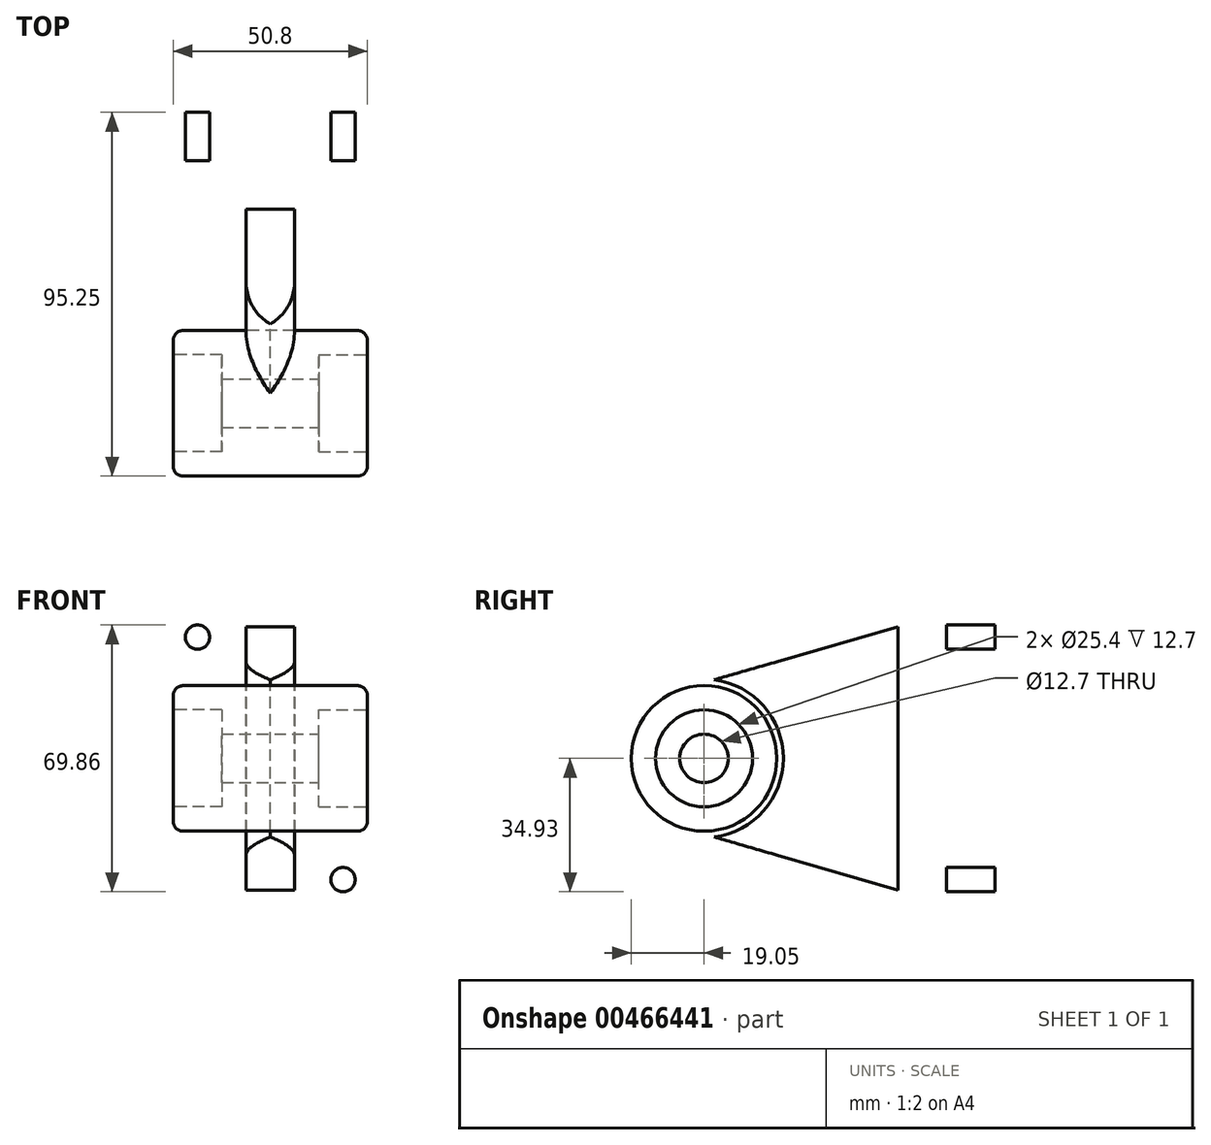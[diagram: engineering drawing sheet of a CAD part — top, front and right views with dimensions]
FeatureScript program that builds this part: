
annotation { "Feature Type Name" : "Feature", "Feature Type Description" : "" }
export const myFeature = defineFeature(function(context is Context, id is Id, definition is map)
    precondition{}
    {
        {
            var Q0;
            Q0=qCreatedBy(makeId("Front.planeOp"),FACE);
            var sketch = newSketch(context, id + "F0", { "sketchPlane" : qUnion([Q0])});
            skLineSegment(sketch, "E0.bottom", {"start": v(-25.4, 38.1) * mm, "end": v(25.4, 38.1) * mm});
            skLineSegment(sketch, "E0.top", {"start": v(-25.4, -38.1) * mm, "end": v(25.4, -38.1) * mm});
            skLineSegment(sketch, "E0.left", {"start": v(-25.4, 38.1) * mm, "end": v(-25.4, -38.1) * mm});
            skLineSegment(sketch, "E0.right", {"start": v(25.4, 38.1) * mm, "end": v(25.4, -38.1) * mm});
            skSolve(sketch);
        }
        {
            var Q0;
            Q0=makeQuery(id+"F0.imprint","IMPRINT",FACE,{"disambiguationData":[TD([[makeQuery(id+"F0.imprint","IMPRINT",EDGE,{"derivedFrom":sQuery(id+"F0.wireOp",EDGE,"E0.bottom")}),-1.0]])]});
            extrude(context, id + "F1", {"entities" : qUnion([Q0]), "depth" : 12.7 * mm});
        }
        {
            var Q0;
            Q0=qCreatedBy(makeId("Right.planeOp"),FACE);
            var sketch = newSketch(context, id + "F2", { "sketchPlane" : qUnion([Q0])});
            skCircle(sketch, "E1", {"center": v(-76.2, 0) * mm, "radius": 19.05 * mm});
            skSolve(sketch);
        }
        {
            var Q0;
            Q0=makeQuery(id+"F2.imprint","IMPRINT",FACE,{"disambiguationData":[TD([[makeQuery(id+"F2.imprint","IMPRINT",EDGE,{"derivedFrom":sQuery(id+"F2.wireOp",EDGE,"E1")}),1.0]])]});
            extrude(context, id + "F3", {"entities" : qUnion([Q0]), "depth" : 25.4 * mm, "hasSecondDirection" : true, "secondDirectionOppositeDirection" : true, "secondDirectionDepth" : 25.4 * mm});
        }
        {
            var Q0;
            Q0=makeQuery(id+"F3.opExtrude","CAP_FACE",FACE,{"disambiguationData":[OSD([sQuery(id+"F2.wireOp",EDGE,"E1")])],"isStart":false});
            var sketch = newSketch(context, id + "F4", { "sketchPlane" : qUnion([Q0])});
            skCircle(sketch, "E2", {"center": v(-76.2, 0) * mm, "radius": 6.35 * mm});
            skCircle(sketch, "E3", {"center": v(-76.2, 0) * mm, "radius": 12.7 * mm});
            skSolve(sketch);
        }
        {
            var Q0;
            Q0=makeQuery(id+"F4.imprint","IMPRINT",FACE,{"disambiguationData":[TD([[makeQuery(id+"F4.imprint","IMPRINT",EDGE,{"derivedFrom":sQuery(id+"F4.wireOp",EDGE,"E2")}),1.0]])]});
            extrude(context, id + "F5", {"entities" : qUnion([Q0]), "operationType" : NewBodyOperationType.REMOVE, "endBound" : BoundingType.THROUGH_ALL, "oppositeDirection" : true, "depth" : 25.4 * mm});
        }
        {
            var Q0;
            Q0=makeQuery(id+"F3.opExtrude","CAP_FACE",FACE,{"disambiguationData":[OSD([sQuery(id+"F2.wireOp",EDGE,"E1")])],"isStart":false});
            var sketch = newSketch(context, id + "F6", { "sketchPlane" : qUnion([Q0])});
            skCircle(sketch, "E4", {"center": v(-76.2, 0) * mm, "radius": 12.7 * mm});
            skSolve(sketch);
        }
        {
            var Q0;
            Q0=makeQuery(id+"F6.imprint","IMPRINT",FACE,{"disambiguationData":[TD([[makeQuery(id+"F6.imprint","IMPRINT",EDGE,{"derivedFrom":sQuery(id+"F6.wireOp",EDGE,"E4")}),1.0]])]});
            extrude(context, id + "F7", {"entities" : qUnion([Q0]), "operationType" : NewBodyOperationType.REMOVE, "oppositeDirection" : true, "depth" : 12.7 * mm});
        }
        {
            var Q0;
            Q0=makeQuery(id+"F3.opExtrude","CAP_FACE",FACE,{"disambiguationData":[OSD([sQuery(id+"F2.wireOp",EDGE,"E1")])],"isStart":true});
            var sketch = newSketch(context, id + "F8", { "sketchPlane" : qUnion([Q0])});
            skCircle(sketch, "E5", {"center": v(76.2, 0) * mm, "radius": 12.7 * mm});
            skSolve(sketch);
        }
        {
            var Q0;
            Q0=makeQuery(id+"F8.imprint","IMPRINT",FACE,{"disambiguationData":[TD([[makeQuery(id+"F8.imprint","IMPRINT",EDGE,{"derivedFrom":sQuery(id+"F8.wireOp",EDGE,"E5")}),1.0]])]});
            extrude(context, id + "F9", {"entities" : qUnion([Q0]), "operationType" : NewBodyOperationType.REMOVE, "oppositeDirection" : true, "depth" : 12.7 * mm});
        }
        {
            var Q0;
            Q0=qCreatedBy(makeId("Right.planeOp"),FACE);
            var sketch = newSketch(context, id + "F10", { "sketchPlane" : qUnion([Q0])});
            skLineSegment(sketch, "E6", {"start": v(-81.47, 18.3) * mm, "end": v(-12.7, 38.1) * mm});
            skLineSegment(sketch, "E7", {"start": v(-81.47, -18.3) * mm, "end": v(-12.7, -38.1) * mm});
            skLineSegment(sketch, "E8", {"start": v(-12.7, 38.1) * mm, "end": v(-12.7, -38.1) * mm});
            skArc(sketch, "E9", {"start": v(-81.47, -18.3) * mm, "mid": v(-57.15, 0) * mm, "end": v(-81.47, 18.3) * mm});
            skSolve(sketch);
        }
        {
            var Q0;
            Q0=makeQuery(id+"F10.imprint","IMPRINT",FACE,{"disambiguationData":[TD([[makeQuery(id+"F10.imprint","IMPRINT",EDGE,{"derivedFrom":sQuery(id+"F10.wireOp",EDGE,"E6")}),-1.0]])]});
            extrude(context, id + "F11", {"entities" : qUnion([Q0]), "depth" : 6.35 * mm, "hasSecondDirection" : true, "secondDirectionOppositeDirection" : true, "secondDirectionDepth" : 6.35 * mm});
        }
        {
            var Q0;
            Q0=makeQuery(id+"F11.opExtrude","CAP_EDGE",EDGE,{"disambiguationData":[OSD([sQuery(id+"F10.wireOp",EDGE,"E8")])],"isStart":false});
            var Q1;
            Q1=makeQuery(id+"F11.opExtrude","CAP_EDGE",EDGE,{"disambiguationData":[OSD([sQuery(id+"F10.wireOp",EDGE,"E8")])],"isStart":true});
            var Q2;
            Q2=makeQuery(id+"F11.opExtrude","CAP_EDGE",EDGE,{"disambiguationData":[OSD([sQuery(id+"F10.wireOp",EDGE,"E9")])],"isStart":false});
            var Q3;
            Q3=makeQuery(id+"F11.opExtrude","CAP_EDGE",EDGE,{"disambiguationData":[OSD([sQuery(id+"F10.wireOp",EDGE,"E9")])],"isStart":true});
            fillet(context, id + "F12", {"entities" : qUnion([Q0, Q1, Q2, Q3]), "radius" : 12.7 * mm, "tangentPropagation" : true, "allowEdgeOverflow" : false});
        }
        {
            var Q0;
            Q0=makeQuery(id+"F3.opExtrude","CAP_EDGE",EDGE,{"disambiguationData":[OSD([sQuery(id+"F2.wireOp",EDGE,"E1")])],"isStart":false});
            var Q1;
            Q1=makeQuery(id+"F3.opExtrude","CAP_EDGE",EDGE,{"disambiguationData":[OSD([sQuery(id+"F2.wireOp",EDGE,"E1")])],"isStart":true});
            fillet(context, id + "F13", {"entities" : qUnion([Q0, Q1]), "radius" : 2.54 * mm, "tangentPropagation" : true, "allowEdgeOverflow" : false});
        }
        {
            var Q0;
            Q0=makeQuery(id+"F1.opExtrude","CAP_FACE",FACE,{"disambiguationData":[OSD([sQuery(id+"F0.wireOp",EDGE,"E0.bottom"),sQuery(id+"F0.wireOp",EDGE,"E0.top"),sQuery(id+"F0.wireOp",EDGE,"E0.left"),sQuery(id+"F0.wireOp",EDGE,"E0.right")])],"isStart":true});
            var sketch = newSketch(context, id + "F14", { "sketchPlane" : qUnion([Q0])});
            skCircle(sketch, "E10", {"center": v(19.05, -31.75) * mm, "radius": 3.18 * mm});
            skCircle(sketch, "E11.MirrorC", {"center": v(-19.05, -31.75) * mm, "radius": 3.18 * mm});
            skCircle(sketch, "E12.MirrorC", {"center": v(-19.05, 31.75) * mm, "radius": 3.18 * mm});
            skCircle(sketch, "E13.MirrorC", {"center": v(19.05, 31.75) * mm, "radius": 3.18 * mm});
            skSolve(sketch);
        }
        {
            var Q0;
            Q0=makeQuery(id+"F14.imprint","IMPRINT",FACE,{"disambiguationData":[TD([[makeQuery(id+"F14.imprint","IMPRINT",EDGE,{"derivedFrom":sQuery(id+"F14.wireOp",EDGE,"E13.MirrorC")}),-1.0]])]});
            var Q1;
            Q1=makeQuery(id+"F14.imprint","IMPRINT",FACE,{"disambiguationData":[TD([[makeQuery(id+"F14.imprint","IMPRINT",EDGE,{"derivedFrom":sQuery(id+"F14.wireOp",EDGE,"E10")}),1.0]])]});
            var Q2;
            Q2=makeQuery(id+"F14.imprint","IMPRINT",FACE,{"disambiguationData":[TD([[makeQuery(id+"F14.imprint","IMPRINT",EDGE,{"derivedFrom":sQuery(id+"F14.wireOp",EDGE,"E11.MirrorC")}),-1.0]])]});
            var Q3;
            Q3=makeQuery(id+"F14.imprint","IMPRINT",FACE,{"disambiguationData":[TD([[makeQuery(id+"F14.imprint","IMPRINT",EDGE,{"derivedFrom":sQuery(id+"F14.wireOp",EDGE,"E12.MirrorC")}),1.0]])]});
            extrude(context, id + "F15", {"entities" : qUnion([Q0, Q1, Q2, Q3]), "operationType" : NewBodyOperationType.REMOVE, "oppositeDirection" : true, "depth" : 25.4 * mm});
        }
    });
